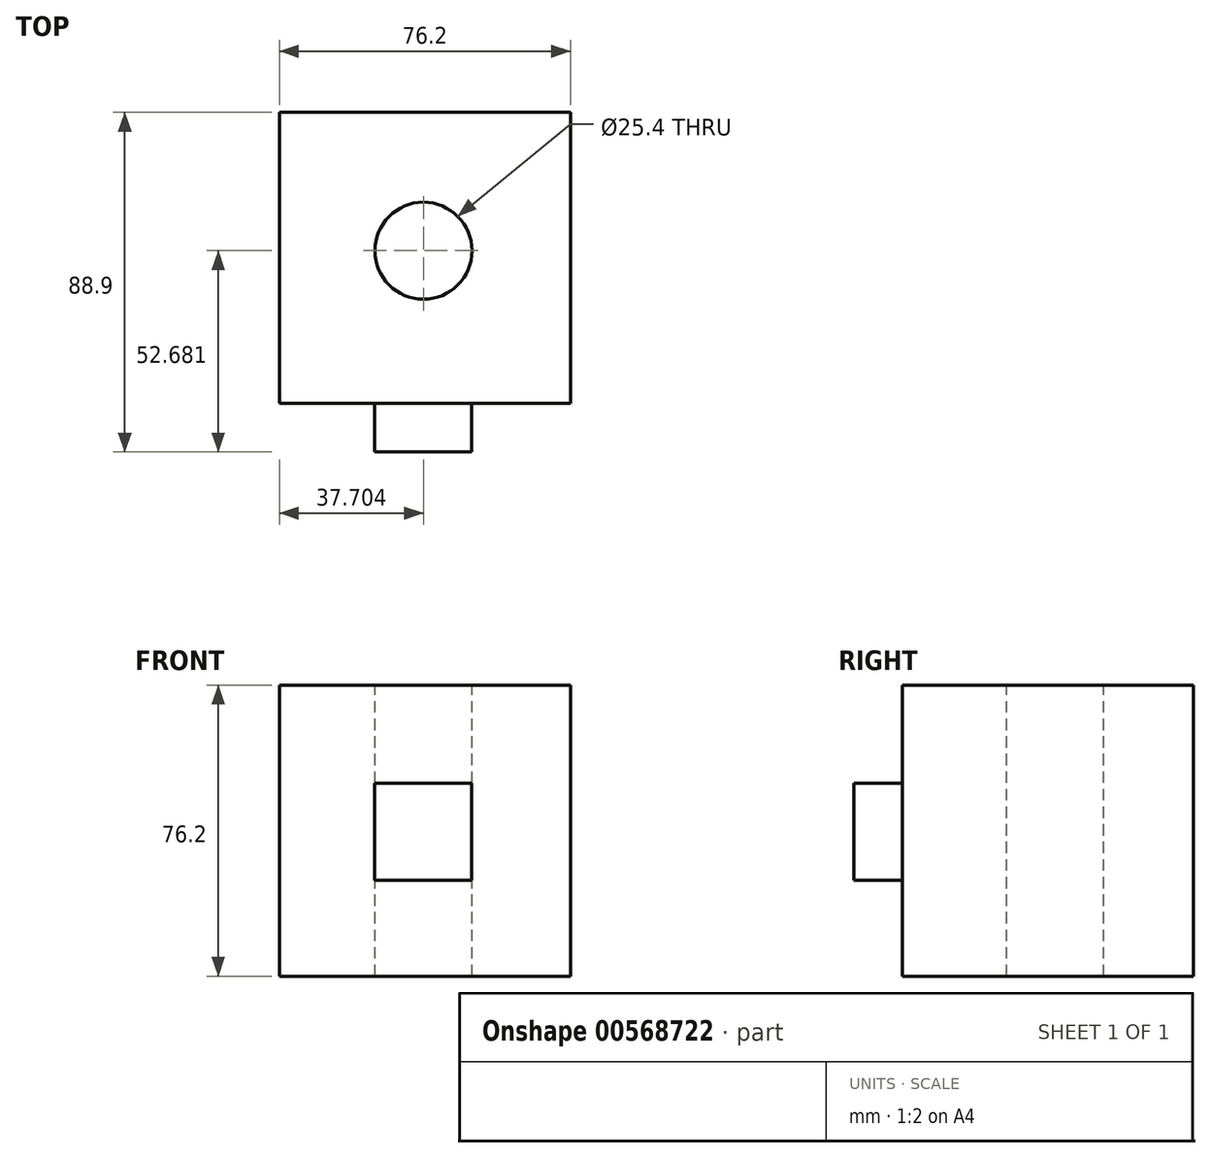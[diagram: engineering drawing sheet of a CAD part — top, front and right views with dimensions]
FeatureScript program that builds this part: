
annotation { "Feature Type Name" : "Feature", "Feature Type Description" : "" }
export const myFeature = defineFeature(function(context is Context, id is Id, definition is map)
    precondition{}
    {
        {
            var Q0;
            Q0=qCreatedBy(makeId("Front.planeOp"),FACE);
            var sketch = newSketch(context, id + "F0", { "sketchPlane" : qUnion([Q0])});
            skLineSegment(sketch, "E0.bottom", {"start": v(0, 0) * mm, "end": v(76.2, 0) * mm});
            skLineSegment(sketch, "E0.top", {"start": v(0, 76.2) * mm, "end": v(76.2, 76.2) * mm});
            skLineSegment(sketch, "E0.left", {"start": v(0, 0) * mm, "end": v(0, 76.2) * mm});
            skLineSegment(sketch, "E0.right", {"start": v(76.2, 0) * mm, "end": v(76.2, 76.2) * mm});
            skSolve(sketch);
        }
        {
            var Q0;
            Q0=makeQuery(id+"F0.imprint","IMPRINT",FACE,{"disambiguationData":[TD([[makeQuery(id+"F0.imprint","IMPRINT",EDGE,{"derivedFrom":sQuery(id+"F0.wireOp",EDGE,"E0.bottom")}),1.0]])]});
            extrude(context, id + "F1", {"entities" : qUnion([Q0]), "depth" : 76.2 * mm, "offsetDistance" : 25.4 * mm});
        }
        {
            var Q0;
            Q0=makeQuery(id+"F1.opExtrude","SWEPT_FACE",FACE,{"disambiguationData":[OSD([sQuery(id+"F0.wireOp",EDGE,"E0.top")])]});
            var sketch = newSketch(context, id + "F2", { "sketchPlane" : qUnion([Q0])});
            skPoint(sketch, "E1", {"position": v(37.7, -36.22) * mm});
            skSolve(sketch);
        }
        {
            var Q0;
            Q0=sQuery(id+"F2.wireOp",VERTEX,"E1");
            var Q1;
            Q1=makeQuery(id+"F1.opExtrude","SWEPT_BODY",BODY,{"disambiguationData":[OSD([sQuery(id+"F0.wireOp",EDGE,"E0.bottom"),sQuery(id+"F0.wireOp",EDGE,"E0.top"),sQuery(id+"F0.wireOp",EDGE,"E0.left"),sQuery(id+"F0.wireOp",EDGE,"E0.right")])]});
            hole(context, id + "F3", {"style" : HoleStyle.SIMPLE, "endStyle" : HoleEndStyle.THROUGH, "holeDiameter" : 25.4 * mm, "isTappedThrough" : true, "tappedDepth" : 12.7 * mm, "tapClearance" : 3, "locations" : qUnion([Q0]), "scope" : qUnion([Q1])});
        }
        {
            var Q0;
            Q0=makeQuery(id+"F1.opExtrude","CAP_FACE",FACE,{"disambiguationData":[OSD([sQuery(id+"F0.wireOp",EDGE,"E0.bottom"),sQuery(id+"F0.wireOp",EDGE,"E0.top"),sQuery(id+"F0.wireOp",EDGE,"E0.left"),sQuery(id+"F0.wireOp",EDGE,"E0.right")])],"isStart":false});
            var sketch = newSketch(context, id + "F4", { "sketchPlane" : qUnion([Q0])});
            skLineSegment(sketch, "E2.bottom", {"start": v(24.95, 25.05) * mm, "end": v(50.35, 25.05) * mm});
            skLineSegment(sketch, "E2.top", {"start": v(24.95, 50.45) * mm, "end": v(50.35, 50.45) * mm});
            skLineSegment(sketch, "E2.left", {"start": v(24.95, 25.05) * mm, "end": v(24.95, 50.45) * mm});
            skLineSegment(sketch, "E2.right", {"start": v(50.35, 25.05) * mm, "end": v(50.35, 50.45) * mm});
            skSolve(sketch);
        }
        {
            var Q0;
            Q0=makeQuery(id+"F4.imprint","IMPRINT",FACE,{"disambiguationData":[TD([[makeQuery(id+"F4.imprint","IMPRINT",EDGE,{"derivedFrom":sQuery(id+"F4.wireOp",EDGE,"E2.bottom")}),1.0]])]});
            extrude(context, id + "F5", {"entities" : qUnion([Q0]), "operationType" : NewBodyOperationType.ADD, "depth" : 12.7 * mm, "offsetDistance" : 25.4 * mm});
        }
        {
            var Q0;
            Q0=makeQuery(id+"F1.opExtrude","SWEPT_FACE",FACE,{"disambiguationData":[OSD([sQuery(id+"F0.wireOp",EDGE,"E0.right")])]});
            var sketch = newSketch(context, id + "F6", { "sketchPlane" : qUnion([Q0])});
            skSolve(sketch);
        }
        {
            var Q0;
            {var subQ0=sQuery(id+"F0.wireOp",EDGE,"E0.right");Q0=makeQuery(id+"F6.imprint","IMPRINT",FACE,{"disambiguationData":[TD([[makeQuery(id+"F6.imprint","IMPRINT",EDGE,{"derivedFrom":makeQuery(id+"F1.opExtrude","CAP_EDGE",EDGE,{"disambiguationData":[OSD([subQ0])],"isStart":true})}),1.0]])]});}
            var sketch = newSketch(context, id + "F7", { "sketchPlane" : qUnion([Q0])});
            skCircle(sketch, "E3", {"center": v(-38.1, 38.1) * mm, "radius": 12.7 * mm});
            skSolve(sketch);
        }
        {
            var Q0;
            Q0=sQuery(id+"F7.wireOp",EDGE,"E3");
            extrude(context, id + "F8", {"bodyType" : ToolBodyType.SURFACE, "surfaceEntities" : qUnion([Q0]), "depth" : 12.7 * mm, "offsetDistance" : 25.4 * mm});
        }
    });
